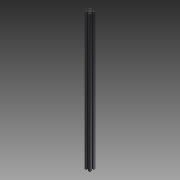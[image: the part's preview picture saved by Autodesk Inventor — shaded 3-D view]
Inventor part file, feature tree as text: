
AUTODESK INVENTOR PART (.ipt)
format: ipt  version: 2011 SP1 (Build 150282100, 282)  size: 185,856 bytes
history: native  units: mm
features: other x21, sketch x3, hole x2, extrude x1, pattern_linear x1
ambient origin geometry x8: Origin, YZ Plane, XZ Plane, XY Plane, X Axis, Y Axis, Z Axis, Center Point
bodies: Solid1 (feature_tree)
feature tree (28):
  extrude  "Extrusion1"  Depth=20.0mm
  hole  "Hole1"  [1 undecoded]
  hole  "Hole2"  [1 undecoded]
  pattern_linear  "Rectangular Pattern1"  [2 undecoded]
  other  "C1_XY"
  other  "C1_YZ"
  other  "C1_ZX"
  other  "C1_X"
  other  "C1_Y"
  other  "C1_Z"
  other  "C1_Center"
  other  "to_frame_cap1_XY"
  other  "to_frame_cap1_YZ"
  other  "to_frame_cap1_ZX"
  other  "to_frame_cap1_X"
  other  "to_frame_cap1_Y"
  other  "to_frame_cap1_Z"
  other  "to_frame_cap1_Center"
  other  "to_frame_cap2_XY"
  other  "to_frame_cap2_YZ"
  other  "to_frame_cap2_ZX"
  other  "to_frame_cap2_X"
  other  "to_frame_cap2_Y"
  other  "to_frame_cap2_Z"
  other  "to_frame_cap2_Center"
  sketch  "Sketch_1"  dims[d0=750.0mm d1=0.0mm]
  sketch  "Sketch2"  dims[d2=6.8mm d3=6.0mm d4=4.0mm d5=2.0mm d6=90.0deg d7=750.0mm d8=0.0mm]
  sketch  "Sketch3"  dims[d9=4.2mm d10=6.0mm d11=4.0mm d12=2.0mm d13=90.0deg d14=750.0mm d15=0.0mm d16=20.0mm d18=23.2mm d19=20.0mm d21=23.2mm d22=0.0mm d23=0.0mm d24=0.0mm]
note: 4 required parameter values undecoded (feature->parameter linkage not recoverable at this tier; creation-order binding heuristic only, values carry confidence <= 0.55)
